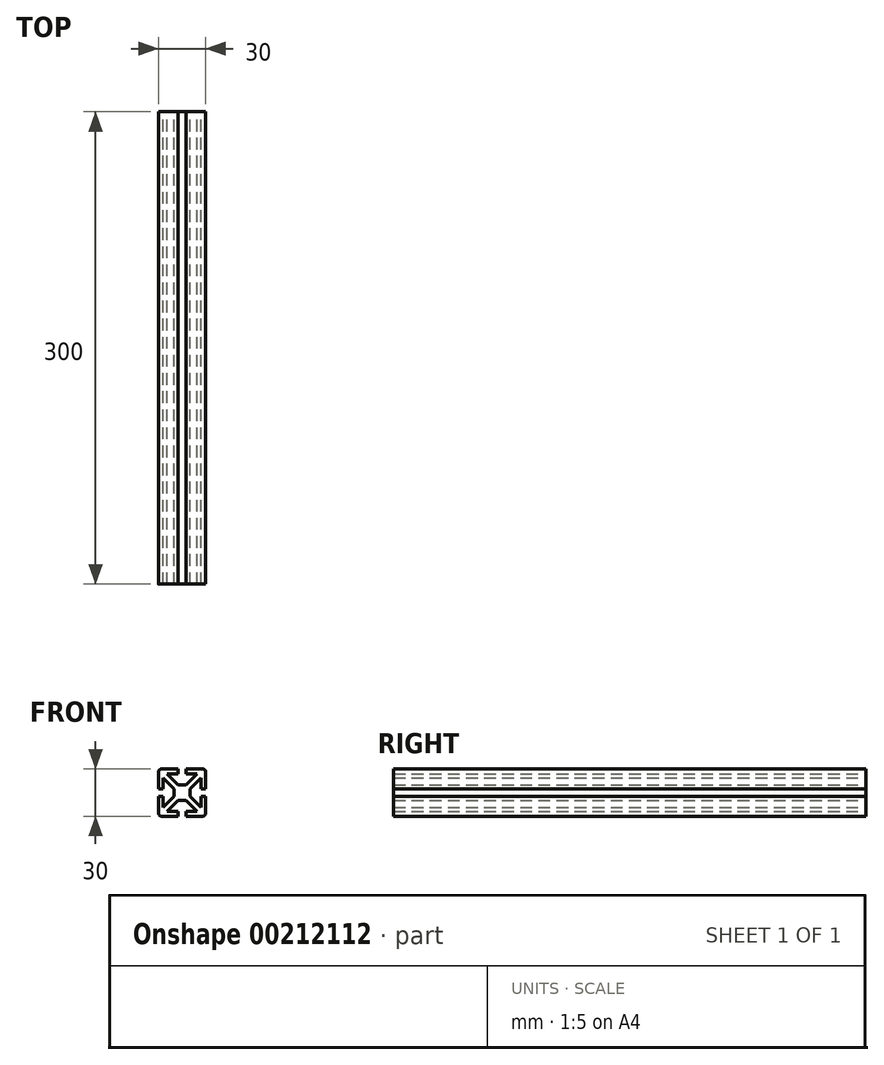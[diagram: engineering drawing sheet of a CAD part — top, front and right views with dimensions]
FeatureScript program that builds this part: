
annotation { "Feature Type Name" : "Feature", "Feature Type Description" : "" }
export const myFeature = defineFeature(function(context is Context, id is Id, definition is map)
    precondition{}
    {
        {
            var Q0;
            Q0=qCreatedBy(makeId("Front.planeOp"),FACE);
            var sketch = newSketch(context, id + "F0", { "sketchPlane" : qUnion([Q0])});
            skLineSegment(sketch, "E0", {"start": v(17.5, 30) * mm, "end": v(28, 30) * mm});
            skLineSegment(sketch, "E1", {"start": v(30, 28) * mm, "end": v(30, 17.5) * mm});
            skLineSegment(sketch, "E2", {"start": v(30, 17.5) * mm, "end": v(27, 17.5) * mm});
            skLineSegment(sketch, "E3", {"start": v(27, 17.5) * mm, "end": v(27, 24.5) * mm});
            skLineSegment(sketch, "E4", {"start": v(27, 24.5) * mm, "end": v(20, 17.5) * mm});
            skLineSegment(sketch, "E5", {"start": v(17.5, 30) * mm, "end": v(17.5, 27) * mm});
            skLineSegment(sketch, "E6", {"start": v(17.5, 27) * mm, "end": v(24.5, 27) * mm});
            skLineSegment(sketch, "E7", {"start": v(24.5, 27) * mm, "end": v(17.5, 20) * mm});
            skLineSegment(sketch, "E8", {"start": v(20, 17.5) * mm, "end": v(20, 12.5) * mm});
            skLineSegment(sketch, "E9", {"start": v(20, 12.5) * mm, "end": v(27, 5.5) * mm});
            skLineSegment(sketch, "E10", {"start": v(27, 5.5) * mm, "end": v(27, 12.5) * mm});
            skLineSegment(sketch, "E11", {"start": v(27, 12.5) * mm, "end": v(30, 12.5) * mm});
            skLineSegment(sketch, "E12", {"start": v(30, 12.5) * mm, "end": v(30, 2) * mm});
            skLineSegment(sketch, "E13", {"start": v(28, 0) * mm, "end": v(17.5, 0) * mm});
            skLineSegment(sketch, "E14", {"start": v(17.5, 0) * mm, "end": v(17.5, 3) * mm});
            skLineSegment(sketch, "E15", {"start": v(17.5, 3) * mm, "end": v(24.5, 3) * mm});
            skLineSegment(sketch, "E16", {"start": v(24.5, 3) * mm, "end": v(17.5, 10) * mm});
            skLineSegment(sketch, "E17", {"start": v(17.5, 10) * mm, "end": v(12.5, 10) * mm});
            skLineSegment(sketch, "E18", {"start": v(12.5, 10) * mm, "end": v(5.5, 3) * mm});
            skLineSegment(sketch, "E19", {"start": v(5.5, 3) * mm, "end": v(12.5, 3) * mm});
            skLineSegment(sketch, "E20", {"start": v(12.5, 3) * mm, "end": v(12.5, 0) * mm});
            skLineSegment(sketch, "E21", {"start": v(12.5, 0) * mm, "end": v(2, 0) * mm});
            skLineSegment(sketch, "E22", {"start": v(0, 2) * mm, "end": v(0, 12.5) * mm});
            skLineSegment(sketch, "E23", {"start": v(0, 12.5) * mm, "end": v(3, 12.5) * mm});
            skLineSegment(sketch, "E24", {"start": v(3, 12.5) * mm, "end": v(3, 5.5) * mm});
            skLineSegment(sketch, "E25", {"start": v(3, 5.5) * mm, "end": v(10, 12.5) * mm});
            skLineSegment(sketch, "E26", {"start": v(10, 12.5) * mm, "end": v(10, 17.5) * mm});
            skLineSegment(sketch, "E27", {"start": v(10, 17.5) * mm, "end": v(3, 24.5) * mm});
            skLineSegment(sketch, "E28", {"start": v(3, 24.5) * mm, "end": v(3, 17.5) * mm});
            skLineSegment(sketch, "E29", {"start": v(3, 17.5) * mm, "end": v(0, 17.5) * mm});
            skLineSegment(sketch, "E30", {"start": v(0, 17.5) * mm, "end": v(0, 28) * mm});
            skLineSegment(sketch, "E31", {"start": v(2, 30) * mm, "end": v(12.5, 30) * mm});
            skLineSegment(sketch, "E32", {"start": v(12.5, 30) * mm, "end": v(12.5, 27) * mm});
            skLineSegment(sketch, "E33", {"start": v(12.5, 27) * mm, "end": v(5.5, 27) * mm});
            skLineSegment(sketch, "E34", {"start": v(5.5, 27) * mm, "end": v(12.5, 20) * mm});
            skLineSegment(sketch, "E35", {"start": v(12.5, 20) * mm, "end": v(17.5, 20) * mm});
            skPoint(sketch, "E36.visualSharp", {"position": v(0, 30) * mm});
            skArc(sketch, "E36.filletArc", {"start": v(2, 30) * mm, "mid": v(0.59, 29.41) * mm, "end": v(0, 28) * mm});
            skPoint(sketch, "E37.visualSharp", {"position": v(30, 30) * mm});
            skArc(sketch, "E37.filletArc", {"start": v(30, 28) * mm, "mid": v(29.41, 29.41) * mm, "end": v(28, 30) * mm});
            skPoint(sketch, "E38.visualSharp", {"position": v(30, 0) * mm});
            skArc(sketch, "E38.filletArc", {"start": v(28, 0) * mm, "mid": v(29.41, 0.59) * mm, "end": v(30, 2) * mm});
            skPoint(sketch, "E39.visualSharp", {"position": v(0, 0) * mm});
            skArc(sketch, "E39.filletArc", {"start": v(0, 2) * mm, "mid": v(0.59, 0.59) * mm, "end": v(2, 0) * mm});
            skSolve(sketch);
        }
        {
            var Q0;
            Q0 = qSketchRegion(id + "F0", true);
            extrude(context, id + "F1", {"entities" : qUnion([Q0]), "depth" : 300 * mm});
        }
    });
